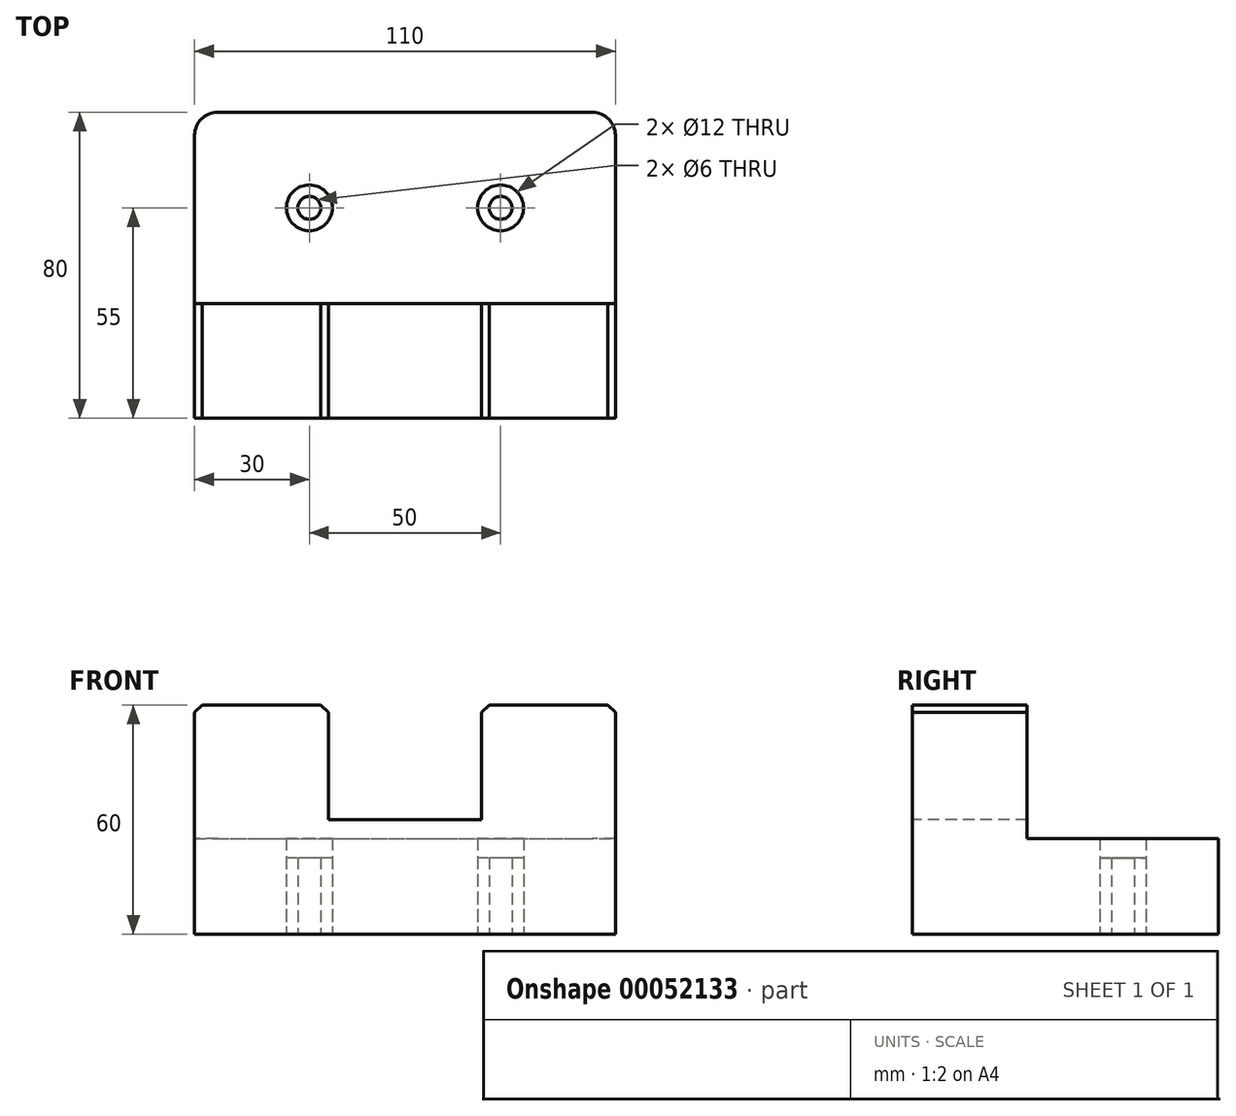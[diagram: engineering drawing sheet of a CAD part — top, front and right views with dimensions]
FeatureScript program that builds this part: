
annotation { "Feature Type Name" : "Feature", "Feature Type Description" : "" }
export const myFeature = defineFeature(function(context is Context, id is Id, definition is map)
    precondition{}
    {
        {
            var Q0;
            Q0=qCreatedBy(makeId("Top.planeOp"),FACE);
            var sketch = newSketch(context, id + "F0", { "sketchPlane" : qUnion([Q0])});
            skLineSegment(sketch, "E0.bottom", {"start": v(6, 0) * mm, "end": v(104, 0) * mm});
            skLineSegment(sketch, "E0.top", {"start": v(0, 80) * mm, "end": v(110, 80) * mm});
            skLineSegment(sketch, "E0.left", {"start": v(0, 6) * mm, "end": v(0, 80) * mm});
            skLineSegment(sketch, "E0.right", {"start": v(110, 6) * mm, "end": v(110, 80) * mm});
            skCircle(sketch, "E1", {"center": v(30, 55) * mm, "radius": 6 * mm});
            skCircle(sketch, "E2", {"center": v(80, 55) * mm, "radius": 6 * mm});
            skCircle(sketch, "E3", {"center": v(30, 55) * mm, "radius": 3 * mm});
            skCircle(sketch, "E4", {"center": v(80, 55) * mm, "radius": 3 * mm});
            skLineSegment(sketch, "E5", {"start": v(0, 30) * mm, "end": v(110, 30) * mm});
            skLineSegment(sketch, "E6", {"start": v(35, 30) * mm, "end": v(35, 0) * mm});
            skLineSegment(sketch, "E7", {"start": v(75, 30) * mm, "end": v(75, 0) * mm});
            skPoint(sketch, "E8.visualSharp", {"position": v(110, 0) * mm});
            skLineSegment(sketch, "E9", {"start": v(110, 6) * mm, "end": v(110, 0) * mm});
            skLineSegment(sketch, "E10", {"start": v(104, 0) * mm, "end": v(110, 0) * mm});
            skLineSegment(sketch, "E11", {"start": v(6, 0) * mm, "end": v(0, 0) * mm});
            skLineSegment(sketch, "E12", {"start": v(0, 6) * mm, "end": v(0, 0) * mm});
            skSolve(sketch);
        }
        {
            var Q0;
            Q0=makeQuery(id+"F0.imprint","IMPRINT",FACE,{"disambiguationData":[TD([[makeQuery(id+"F0.imprint","IMPRINT",EDGE,{"derivedFrom":sQuery(id+"F0.wireOp",EDGE,"E1")}),1.0]])]});
            var Q1;
            Q1=makeQuery(id+"F0.imprint","IMPRINT",FACE,{"disambiguationData":[TD([[makeQuery(id+"F0.imprint","IMPRINT",EDGE,{"derivedFrom":sQuery(id+"F0.wireOp",EDGE,"E2")}),1.0]])]});
            extrude(context, id + "F1", {"entities" : qUnion([Q0, Q1]), "depth" : 20 * mm});
        }
        {
            var Q0;
            {var subQ1=sQuery(id+"F0.wireOp",EDGE,"E0.top");Q0=makeQuery(id+"F0.imprint","IMPRINT",FACE,{"disambiguationData":[TD([[makeQuery(id+"F0.imprint","IMPRINT",EDGE,{"derivedFrom":subQ1}),-1.0]])]});}
            extrude(context, id + "F2", {"entities" : qUnion([Q0]), "depth" : 25 * mm});
        }
        {
            var Q0;
            {var subQ3=sQuery(id+"F0.wireOp",EDGE,"E6");Q0=makeQuery(id+"F0.imprint","IMPRINT",FACE,{"disambiguationData":[TD([[makeQuery(id+"F0.imprint","IMPRINT",EDGE,{"derivedFrom":subQ3}),-1.0]])]});}
            var Q1;
            {var subQ3=sQuery(id+"F0.wireOp",EDGE,"E7");Q1=makeQuery(id+"F0.imprint","IMPRINT",FACE,{"disambiguationData":[TD([[makeQuery(id+"F0.imprint","IMPRINT",EDGE,{"derivedFrom":subQ3}),1.0]])]});}
            extrude(context, id + "F3", {"entities" : qUnion([Q0, Q1]), "operationType" : NewBodyOperationType.ADD, "depth" : 60 * mm});
        }
        {
            var Q0;
            {var subQ0=sQuery(id+"F0.wireOp",EDGE,"E6");Q0=makeQuery(id+"F0.imprint","IMPRINT",FACE,{"disambiguationData":[TD([[makeQuery(id+"F0.imprint","IMPRINT",EDGE,{"derivedFrom":subQ0}),1.0]])]});}
            extrude(context, id + "F4", {"entities" : qUnion([Q0]), "operationType" : NewBodyOperationType.ADD, "depth" : 30 * mm});
        }
        {
            var Q0;
            Q0=makeQuery(id+"F3.opExtrude","CAP_EDGE",EDGE,{"disambiguationData":[OSD([sQuery(id+"F0.wireOp",EDGE,"E0.right"),sQuery(id+"F0.wireOp",EDGE,"E9")])],"isStart":false});
            var Q1;
            Q1=makeQuery(id+"F3.opExtrude","CAP_EDGE",EDGE,{"disambiguationData":[OSD([sQuery(id+"F0.wireOp",EDGE,"E7")])],"isStart":false});
            var Q2;
            Q2=makeQuery(id+"F3.opExtrude","CAP_EDGE",EDGE,{"disambiguationData":[OSD([sQuery(id+"F0.wireOp",EDGE,"E6")])],"isStart":false});
            var Q3;
            Q3=makeQuery(id+"F3.opExtrude","CAP_EDGE",EDGE,{"disambiguationData":[OSD([sQuery(id+"F0.wireOp",EDGE,"E0.left"),sQuery(id+"F0.wireOp",EDGE,"E12")])],"isStart":false});
            chamfer(context, id + "F5", {"entities" : qUnion([Q0, Q1, Q2, Q3]), "width" : 2 * mm, "tangentPropagation" : true});
        }
        {
            var Q0;
            Q0=makeQuery(id+"F2.opExtrude","SWEPT_EDGE",EDGE,{"disambiguationData":[OSD([sQuery(id+"F0.wireOp",EDGE,"E0.top"),sQuery(id+"F0.wireOp",EDGE,"E0.left")])]});
            var Q1;
            Q1=makeQuery(id+"F2.opExtrude","SWEPT_EDGE",EDGE,{"disambiguationData":[OSD([sQuery(id+"F0.wireOp",EDGE,"E0.top"),sQuery(id+"F0.wireOp",EDGE,"E0.right")])]});
            fillet(context, id + "F6", {"entities" : qUnion([Q0, Q1]), "radius" : 6 * mm, "tangentPropagation" : true, "allowEdgeOverflow" : false});
        }
    });
